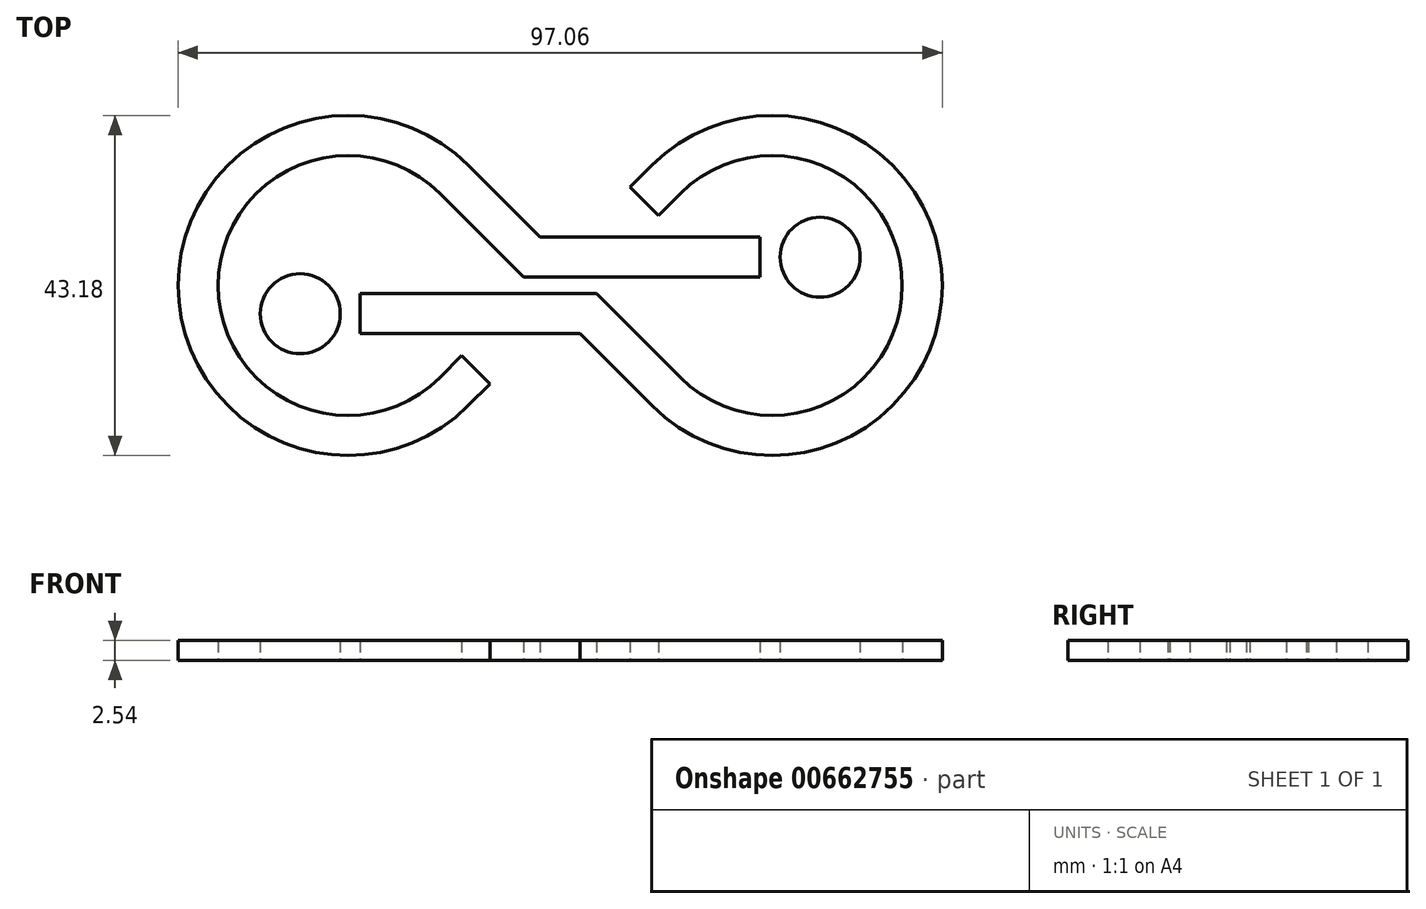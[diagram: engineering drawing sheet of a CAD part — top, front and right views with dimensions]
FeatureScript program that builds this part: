
annotation { "Feature Type Name" : "Feature", "Feature Type Description" : "" }
export const myFeature = defineFeature(function(context is Context, id is Id, definition is map)
    precondition{}
    {
        {
            var Q0;
            Q0=qCreatedBy(makeId("Top.planeOp"),FACE);
            var sketch = newSketch(context, id + "F0", { "sketchPlane" : qUnion([Q0])});
            skLineSegment(sketch, "E0", {"start": v(-5.08, -5.08) * mm, "end": v(5.08, 5.08) * mm});
            skLineSegment(sketch, "E1.MirrorCS", {"start": v(-5.08, 5.08) * mm, "end": v(5.08, -5.08) * mm});
            skSolve(sketch);
        }
        {
            var Q0;
            Q0=qCreatedBy(makeId("Top.planeOp"),FACE);
            var sketch = newSketch(context, id + "F1", { "sketchPlane" : qUnion([Q0])});
            skLineSegment(sketch, "E2.bottom", {"start": v(15.27, 11.67) * mm, "end": v(-11.67, -15.27) * mm});
            skLineSegment(sketch, "E2.top", {"start": v(11.67, 15.27) * mm, "end": v(-15.27, -11.67) * mm});
            skLineSegment(sketch, "E2.left", {"start": v(15.27, 11.67) * mm, "end": v(11.67, 15.27) * mm});
            skLineSegment(sketch, "E2.right", {"start": v(-11.67, -15.27) * mm, "end": v(-15.27, -11.67) * mm});
            skPoint(sketch, "E2.middle", {"position": v(0, 0) * mm});
            skLineSegment(sketch, "E3.MirrorCS", {"start": v(-11.67, 15.27) * mm, "end": v(15.27, -11.67) * mm});
            skLineSegment(sketch, "E4.MirrorCS", {"start": v(11.67, -15.27) * mm, "end": v(15.27, -11.67) * mm});
            skLineSegment(sketch, "E5.MirrorCS", {"start": v(-15.27, 11.67) * mm, "end": v(11.67, -15.27) * mm});
            skLineSegment(sketch, "E6.MirrorCS", {"start": v(-15.27, 11.67) * mm, "end": v(-11.67, 15.27) * mm});
            skArc(sketch, "E7", {"start": v(-15.27, 11.67) * mm, "mid": v(-43.45, 0) * mm, "end": v(-15.27, -11.67) * mm});
            skArc(sketch, "E8", {"start": v(-11.67, 15.27) * mm, "mid": v(-48.53, 0) * mm, "end": v(-11.67, -15.27) * mm});
            skArc(sketch, "E9.MirrorCS", {"start": v(15.27, 11.67) * mm, "mid": v(43.45, 0) * mm, "end": v(15.27, -11.67) * mm});
            skArc(sketch, "E10.MirrorCS", {"start": v(11.67, 15.27) * mm, "mid": v(48.53, 0) * mm, "end": v(11.67, -15.27) * mm});
            skLineSegment(sketch, "E11.bottom", {"start": v(31.75, -0.63) * mm, "end": v(-31.75, -0.63) * mm});
            skLineSegment(sketch, "E11.top", {"start": v(31.75, 0.64) * mm, "end": v(-31.75, 0.63) * mm});
            skLineSegment(sketch, "E11.left", {"start": v(31.75, -0.63) * mm, "end": v(31.75, 0.64) * mm});
            skLineSegment(sketch, "E11.right", {"start": v(-31.75, -0.63) * mm, "end": v(-31.75, 0.64) * mm});
            skSolve(sketch);
        }
        {
            var Q0;
            Q0=qCreatedBy(makeId("Top.planeOp"),FACE);
            var sketch = newSketch(context, id + "F2", { "sketchPlane" : qUnion([Q0])});
            skLineSegment(sketch, "E12.0", {"start": v(15.27, 11.67) * mm, "end": v(12.5, 8.9) * mm});
            skArc(sketch, "E13.0", {"start": v(-11.67, 15.27) * mm, "mid": v(-48.53, 0) * mm, "end": v(-11.67, -15.27) * mm});
            skLineSegment(sketch, "E14.0", {"start": v(-11.67, 15.27) * mm, "end": v(-2.54, 6.13) * mm});
            skArc(sketch, "E15.0", {"start": v(15.27, 11.67) * mm, "mid": v(43.45, 0) * mm, "end": v(15.27, -11.67) * mm});
            skLineSegment(sketch, "E16.0", {"start": v(11.67, 15.27) * mm, "end": v(8.9, 12.5) * mm});
            skArc(sketch, "E17.0", {"start": v(-15.27, 11.67) * mm, "mid": v(-43.45, 0) * mm, "end": v(-15.27, -11.67) * mm});
            skLineSegment(sketch, "E18.0", {"start": v(-15.27, 11.67) * mm, "end": v(-4.64, 1.05) * mm});
            skArc(sketch, "E19.0", {"start": v(11.67, 15.27) * mm, "mid": v(48.53, 0) * mm, "end": v(11.67, -15.27) * mm});
            skPoint(sketch, "E20", {"position": v(0, 3.6) * mm});
            skPoint(sketch, "E21", {"position": v(0, -3.6) * mm});
            skLineSegment(sketch, "E22.bottom", {"start": v(25.4, 1.05) * mm, "end": v(-4.64, 1.05) * mm});
            skLineSegment(sketch, "E22.top", {"start": v(25.4, 6.13) * mm, "end": v(-2.54, 6.13) * mm});
            skLineSegment(sketch, "E22.left", {"start": v(25.4, 1.05) * mm, "end": v(25.4, 6.13) * mm});
            skLineSegment(sketch, "E23.MirrorCS", {"start": v(-25.4, -1.05) * mm, "end": v(-25.4, -6.13) * mm});
            skLineSegment(sketch, "E24.MirrorCS", {"start": v(4.64, -1.05) * mm, "end": v(-25.4, -1.05) * mm});
            skCircle(sketch, "E25", {"center": v(33.02, 3.6) * mm, "radius": 5.08 * mm});
            skPoint(sketch, "E25.centerSnap0", {"position": v(25.4, 3.6) * mm});
            skCircle(sketch, "E26", {"center": v(-33.02, -3.6) * mm, "radius": 5.08 * mm});
            skPoint(sketch, "E26.centerSnap0", {"position": v(-25.4, -3.6) * mm});
            skPoint(sketch, "E27", {"position": v(-2.54, 6.13) * mm});
            skPoint(sketch, "E28", {"position": v(2.54, 6.13) * mm});
            skPoint(sketch, "E29", {"position": v(-2.54, -6.13) * mm});
            skPoint(sketch, "E30", {"position": v(2.54, -6.13) * mm});
            skPoint(sketch, "E31", {"position": v(-9.72, -6.13) * mm});
            skPoint(sketch, "E32", {"position": v(-9.72, 6.13) * mm});
            skPoint(sketch, "E33", {"position": v(9.72, -6.13) * mm});
            skPoint(sketch, "E34", {"position": v(9.72, 6.13) * mm});
            skPoint(sketch, "E35", {"position": v(-4.64, 1.05) * mm});
            skPoint(sketch, "E36", {"position": v(-2.54, 1.05) * mm});
            skPoint(sketch, "E37", {"position": v(2.54, 1.05) * mm});
            skPoint(sketch, "E38", {"position": v(4.64, 1.05) * mm});
            skPoint(sketch, "E39", {"position": v(-4.64, -1.05) * mm});
            skPoint(sketch, "E40", {"position": v(-2.54, -1.05) * mm});
            skPoint(sketch, "E41", {"position": v(2.54, -1.05) * mm});
            skPoint(sketch, "E42", {"position": v(4.64, -1.05) * mm});
            skLineSegment(sketch, "E43.trimOffspring", {"start": v(4.64, -1.05) * mm, "end": v(15.27, -11.67) * mm});
            skLineSegment(sketch, "E44.trimOffspring", {"start": v(-12.5, -8.9) * mm, "end": v(-15.27, -11.67) * mm});
            skPoint(sketch, "E22.right.start.orphan", {"position": v(-25.4, 1.05) * mm});
            skPoint(sketch, "E45.orphan", {"position": v(-25.4, 6.13) * mm});
            skLineSegment(sketch, "E46.trimOffspring", {"start": v(2.54, -6.13) * mm, "end": v(11.67, -15.27) * mm});
            skLineSegment(sketch, "E47.trimOffspring", {"start": v(-8.9, -12.5) * mm, "end": v(-11.67, -15.27) * mm});
            skLineSegment(sketch, "E48.trimOffspring", {"start": v(2.54, -6.13) * mm, "end": v(-25.4, -6.13) * mm});
            skPoint(sketch, "E49.MirrorCS.end.orphan", {"position": v(25.4, -6.13) * mm});
            skPoint(sketch, "E50.orphan", {"position": v(25.4, -1.05) * mm});
            skLineSegment(sketch, "E51", {"start": v(-12.5, -8.9) * mm, "end": v(-8.9, -12.5) * mm});
            skLineSegment(sketch, "E52", {"start": v(12.5, 8.9) * mm, "end": v(8.9, 12.5) * mm});
            skSolve(sketch);
        }
        {
            var Q0;
            Q0=makeQuery(id+"F2.imprint","IMPRINT",FACE,{"disambiguationData":[TD([[makeQuery(id+"F2.imprint","IMPRINT",EDGE,{"derivedFrom":sQuery(id+"F2.wireOp",EDGE,"E13.0")}),1.0]])]});
            var Q1;
            Q1=makeQuery(id+"F2.imprint","IMPRINT",FACE,{"disambiguationData":[TD([[makeQuery(id+"F2.imprint","IMPRINT",EDGE,{"derivedFrom":sQuery(id+"F2.wireOp",EDGE,"E12.0")}),-1.0]])]});
            var Q2;
            Q2=makeQuery(id+"F2.imprint","IMPRINT",FACE,{"disambiguationData":[TD([[makeQuery(id+"F2.imprint","IMPRINT",EDGE,{"derivedFrom":sQuery(id+"F2.wireOp",EDGE,"E25")}),1.0]])]});
            var Q3;
            Q3=makeQuery(id+"F2.imprint","IMPRINT",FACE,{"disambiguationData":[TD([[makeQuery(id+"F2.imprint","IMPRINT",EDGE,{"derivedFrom":sQuery(id+"F2.wireOp",EDGE,"E26")}),1.0]])]});
            extrude(context, id + "F3", {"entities" : qUnion([Q0, Q1, Q2, Q3]), "depth" : 2.54 * mm, "offsetDistance" : 25.4 * mm});
        }
    });
